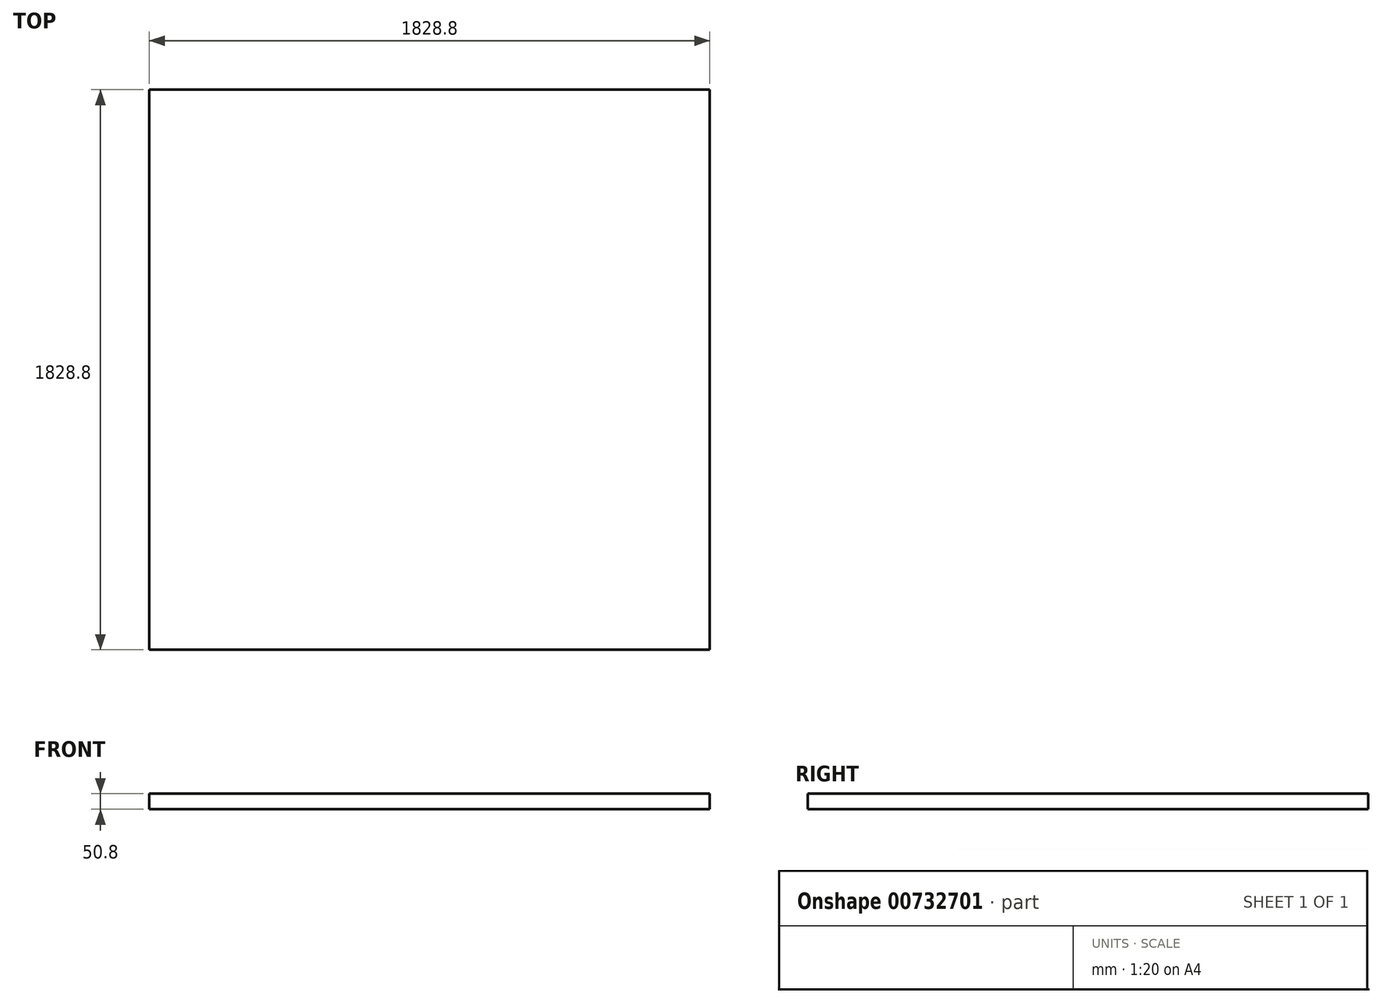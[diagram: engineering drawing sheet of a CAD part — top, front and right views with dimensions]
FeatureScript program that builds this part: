
annotation { "Feature Type Name" : "Feature", "Feature Type Description" : "" }
export const myFeature = defineFeature(function(context is Context, id is Id, definition is map)
    precondition{}
    {
        {
            var Q0;
            Q0=qCreatedBy(makeId("Top.planeOp"),FACE);
            var sketch = newSketch(context, id + "F0", { "sketchPlane" : qUnion([Q0])});
            skLineSegment(sketch, "E0.bottom", {"start": v(0, 0) * mm, "end": v(1828.8, 0) * mm});
            skLineSegment(sketch, "E0.top", {"start": v(0, -1828.8) * mm, "end": v(1828.8, -1828.8) * mm});
            skLineSegment(sketch, "E0.left", {"start": v(0, 0) * mm, "end": v(0, -1828.8) * mm});
            skLineSegment(sketch, "E0.right", {"start": v(1828.8, 0) * mm, "end": v(1828.8, -1828.8) * mm});
            skSolve(sketch);
        }
        {
            var Q0;
            Q0=makeQuery(id+"F0.imprint","IMPRINT",FACE,{"disambiguationData":[TD([[makeQuery(id+"F0.imprint","IMPRINT",EDGE,{"derivedFrom":sQuery(id+"F0.wireOp",EDGE,"E0.bottom")}),-1.0]])]});
            extrude(context, id + "F1", {"entities" : qUnion([Q0]), "depth" : 50.8 * mm, "offsetDistance" : 25.4 * mm});
        }
    });
